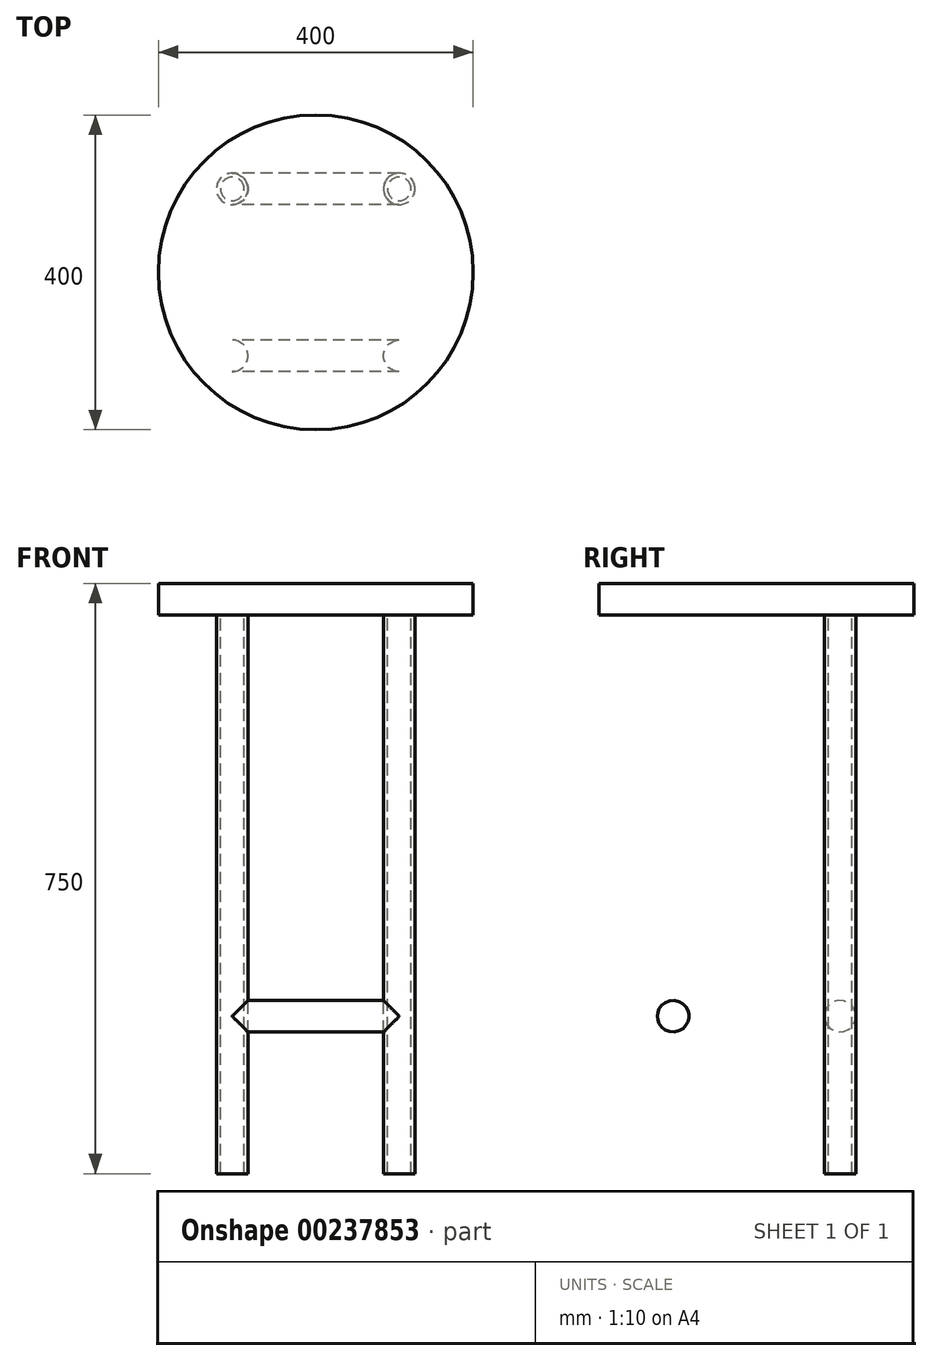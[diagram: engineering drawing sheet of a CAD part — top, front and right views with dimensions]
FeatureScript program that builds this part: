
annotation { "Feature Type Name" : "Feature", "Feature Type Description" : "" }
export const myFeature = defineFeature(function(context is Context, id is Id, definition is map)
    precondition{}
    {
        {
            var Q0;
            Q0=qCreatedBy(makeId("Top.planeOp"),FACE);
            var sketch = newSketch(context, id + "F0", { "sketchPlane" : qUnion([Q0])});
            skCircle(sketch, "E0", {"center": v(0, 0) * mm, "radius": 200 * mm});
            skSolve(sketch);
        }
        {
            var Q0;
            Q0 = qSketchRegion(id + "F0", true);
            extrude(context, id + "F1", {"entities" : qUnion([Q0]), "depth" : 40 * mm});
        }
        {
            var Q0;
            Q0=makeQuery(id+"F1.opExtrude","CAP_FACE",FACE,{"disambiguationData":[OSD([sQuery(id+"F0.wireOp",EDGE,"E0")])],"isStart":true});
            var sketch = newSketch(context, id + "F2", { "sketchPlane" : qUnion([Q0])});
            skLineSegment(sketch, "E1", {"start": v(0, 0) * mm, "end": v(-106.07, 106.07) * mm, "construction": true});
            skCircle(sketch, "E2", {"center": v(-106.07, 106.07) * mm, "radius": 20 * mm});
            skCircle(sketch, "E3", {"center": v(-106.07, 106.07) * mm, "radius": 15 * mm});
            skSolve(sketch);
        }
        {
            var Q0;
            Q0=makeQuery(id+"F2.imprint","IMPRINT",FACE,{"disambiguationData":[TD([[makeQuery(id+"F2.imprint","IMPRINT",EDGE,{"derivedFrom":sQuery(id+"F2.wireOp",EDGE,"E2")}),1.0]])]});
            var Q1;
            Q1=sQuery(id+"F2.wireOp",EDGE,"E2");
            var Q2;
            Q2=sQuery(id+"F2.wireOp",EDGE,"E3");
            extrude(context, id + "F3", {"entities" : qUnion([Q0]), "surfaceEntities" : qUnion([Q1, Q2]), "depth" : 710 * mm});
        }
        {
            var Q0;
            Q0=makeQuery(id+"F3.opExtrude","SWEPT_BODY",BODY,{"disambiguationData":[OSD([sQuery(id+"F2.wireOp",EDGE,"E2"),sQuery(id+"F2.wireOp",EDGE,"E3")])]});
            var Q1;
            Q1=makeQuery(id+"F1.opExtrude","CAP_EDGE",EDGE,{"disambiguationData":[OSD([sQuery(id+"F0.wireOp",EDGE,"E0")])],"isStart":true});
            circularPattern(context, id + "F4", {"entities" : qUnion([Q0]), "axis" : qUnion([Q1]), "angle" : 360 * degree, "instanceCount" : 4, "equalSpace" : true});
        }
        {
            var Q0;
            Q0=qCreatedBy(makeId("Right.planeOp"),FACE);
            var sketch = newSketch(context, id + "F5", { "sketchPlane" : qUnion([Q0])});
            skLineSegment(sketch, "E4", {"start": v(-106.07, 0) * mm, "end": v(-106.07, -510) * mm});
            skCircle(sketch, "E5", {"center": v(-106.07, -510) * mm, "radius": 20 * mm});
            skSolve(sketch);
        }
        {
            var Q0;
            Q0=makeQuery(id+"F5.imprint","IMPRINT",FACE,{"disambiguationData":[TD([[makeQuery(id+"F5.imprint","IMPRINT",EDGE,{"derivedFrom":sQuery(id+"F5.wireOp",EDGE,"E5")}),1.0]])]});
            var Q1;
            Q1=makeQuery(id+"F4.opPattern","COPY",FACE,{"derivedFrom":makeQuery(id+"F3.opExtrude","SWEPT_FACE",FACE,{"disambiguationData":[OSD([sQuery(id+"F2.wireOp",EDGE,"E2")])]}),"instanceName":"1"});
            var Q2;
            Q2=makeQuery(id+"F4.opPattern","COPY",BODY,{"derivedFrom":makeQuery(id+"F3.opExtrude","SWEPT_BODY",BODY,{"disambiguationData":[OSD([sQuery(id+"F2.wireOp",EDGE,"E2"),sQuery(id+"F2.wireOp",EDGE,"E3")])]}),"instanceName":"1"});
            extrude(context, id + "F6", {"entities" : qUnion([Q0]), "endBoundEntityFace" : qUnion([Q1]), "endBoundEntityBody" : qUnion([Q2]), "depth" : 106 * mm, "hasSecondDirection" : true, "secondDirectionOppositeDirection" : true, "secondDirectionDepth" : 106 * mm});
        }
        {
            var Q0;
            Q0=makeQuery(id+"F2.imprint","IMPRINT",FACE,{"disambiguationData":[TD([[makeQuery(id+"F2.imprint","IMPRINT",EDGE,{"derivedFrom":sQuery(id+"F2.wireOp",EDGE,"E2")}),-1.0]])]});
            var sketch = newSketch(context, id + "F7", { "sketchPlane" : qUnion([Q0])});
            skCircle(sketch, "E6.0", {"center": v(106.07, 106.07) * mm, "radius": 20 * mm});
            skCircle(sketch, "E6.1", {"center": v(-106.07, 106.07) * mm, "radius": 20 * mm});
            skSolve(sketch);
        }
        {
            var Q0;
            Q0 = qSketchRegion(id + "F7", true);
            extrude(context, id + "F8", {"entities" : qUnion([Q0]), "operationType" : NewBodyOperationType.REMOVE, "endBound" : BoundingType.THROUGH_ALL, "depth" : 25 * mm});
        }
        {
            var Q0;
            Q0=makeQuery(id+"F6.opExtrude","SWEPT_BODY",BODY,{"disambiguationData":[OSD([sQuery(id+"F5.wireOp",EDGE,"E5")])]});
            var Q1;
            Q1=qCreatedBy(makeId("Front.planeOp"),FACE);
            mirror(context, id + "F9", {"entities" : qUnion([Q0]), "mirrorPlane" : qUnion([Q1])});
        }
    });
